# Revit family: Maxlogic détecteur en boîte arrière de montage en surface
name_source: partatom
category: Fire Alarm Devices
units: mm (PartAtom-declared; Revit-internal decimal feet)

## family parameters
Cut with Voids When Loaded = No
Host = Face
Maintain Annotation Orientation = Yes
OmniClass Number = 23.85.30.21
OmniClass Title = Environmental Detection/Registration
Part Type = Normal
Room Calculation Point = No
Round Connector Dimension = Use Diameter
Shared = No

## types (10) — shared parameters
Adresse ligne 1 = Şerifali Mahallesi Kutup Sokak No:27/1-2-4 Ümraniye TR-34775 İSTANBUL
Boîtier de montage en surface étanche = ML-0121
Couleur = Blanc
Deuxième Matèriel = Plastique
Durée de la garantie de pièces rechange = 2
Durée de la garantie travail = 2
Hauteur Nominal = 106 mm
Largeur Nominal = 51 mm
Longeur Nominal = 106 mm
Manuel d'Installation = https://mavilielektronik.com
Manufacturer = Mavili Elektronik Ticaret A.Ş.
Model = Maxlogic
Numéro de Fax = (+)90 216 466 45 10
Socle Compatible = ML-0140
Socle Compatible 2 = ML-0141
Socle Montage de Surlévé = ML-0150
Tempèrature de Fonctionnement = (-10°C) - (+50°C)
URL = https://www.mavili.com.tr
Voltage de fonctionnement (défaut) = 26 V/DC
zero-valued in all types: Cost, Default Elevation

## per-type parameters (varying)
| type | Cercle Chaleur | Cercle Multi Critère | Charger adresse d'appareil | Code de Performance | Code de Produit | Description | Détection de Radius | Matèriel Principe | Numéro de pose des travaux public | Poids | Sortie d'indicateur | Surface de Montage | Unité de durée de garantie | Voltage fonction d'opération |
| Maxlogic Conventionnelle Détecteur de fumée optique, en boîte arrière de montage en surface | No | No |  | EN 54-7 | ML-2110 | Conventionnelle Conventionnelle Détecteur de fumée optique, en boîte arrière de montage en surface | 6,2 m | Plastique Blanche PC/ABS | 832-106 | 140 gr | MG-4000 | Montage à Plafond | Ans | 10-30V/DC |
| Maxlogic Adressable Détecteur de fumée optique, en boîte arrière de montage en surface | No | No | Appareil d'adressage à Main | EN 54-7 | ML-1110 | Adressable Détecteur de fumée optique , en boîte arrière de montage en surface | 6,2 m | Plastique Blanche PC/ABS | 833-500 | 100 gr | MG-4000.A | Montage à Mur | Ans | 18-33V/DC |
| Maxlogic Adressable détecteur de fumée optique, en boîte arrière de montage en surface,Isolateur de Court-Circuit | No | No | Appareil d'adressage à Main | EN 54-7 / EN 54-17 | ML-1110.SCI | Adressable  Détecteur de fumée optique, en boîte arrière de montage en surface,Isolateur de Court-Circuit | 6,2 m | Plastique Blanche PC/ABS | 833-501 | 100 gr | MG-4000.A | Montage à Plafond | Ans | 18-33V/DC |
| Maxlogic Conventionnelle détecteur de chaleur fixe, en boîte arrière de montage en surface | Yes | No |  | EN 54-5 | ML-2120 | Conventionnelle  Détecteur de chaleur fixe, en boîte arrière de montage en surface | 4,5 m | Plastique Blanche PC/ABS | 832-102 | 135 gr | MG-4000 | Montage à Plafond | Ans | 10-30V/DC |
| Maxlogic Conventionnelle Détecteur de chaleur combiné , en boîte arrière de montage en surface | Yes | No |  | EN 54-5 | ML-2130 | Conventionnelle Détecteur de chaleur combiné , en boîte arrière de montage en surface | 4,5 m | Plastique Blanche PC/ABS | 832-103 | 135 gr | MG-4000 | Montage à Plafond | Year | 10-30V/DC |
| Maxlogic Adressable détecteur de chaleur combiné , en boîte arrière de montage en surface | Yes | No | Appareil d'adressage à Main | EN 54-5 | ML-1130 | Adressable détecteur de chaleur combiné , en boîte arrière de montage en surface | 4,5 m | Plastique Blanche PC/ABS | 833-520 | 95 gr | MG-4000.A | Montage à Plafond | Ans | 18-33V/DC |
| Maxlogic Adressable détecteur de chaleur combiné , en boîte arrière de montage en surface,Isolateur de Court-Circuit | Yes | No | Appareil d'adressage à Main | EN 54-5 / EN 54-17 | ML-1130.SCI | Adressable détecteur de chaleur combiné , en boîte arrière de montage en surface,Isolateur de Court-Circuit | 4,5 m | Plastique Blanche PC/ABS | 833-521 | 95 gr | MG-4000.A | Montage à Plafond | Ans | 18-33V/DC |
| Maxlogic Conventionnelle détecteur de multi-capteur ,en boîte arrière de montage en surface | Yes | Yes |  | EN 54-5 / EN 54-7 | ML-2140 | Conventionnelle détecteur de multi-capteur ,en boîte arrière de montage en surface | 4,5 m | Plastique Blanche PC/ABS | 832-109 | 141 gr | MG-4000 | Montage à Plafond | Ans | 10-30V/DC |
| Maxlogic Adressable Détecteur de multi-capteur, en boîte arrière de montage en surface | Yes | Yes | Appareil d'adressage à Main | EN 54-5 / EN 54-7 / EN 54-17 | ML-1140 | Maxlogic Adressable Détecteur de multi-capteur, en boîte arrière de montage en surface | 4,5 m | Plastique Blanche PC/ABS | 833-530 | 100 gr | MG-4000.A | Montage à Plafond | Ans | 18-33V/DC |
| Maxlogic Adressable Détecteur de multi-capteur, en boîte arrière de montage en surface,Isolateur de Court Circuit | Yes | Yes | Appareil d'adressage à Main | EN 54-5 / EN 54-7 / EN 54-17 | ML-1140.SCI | Adressable Détecteur de multi-capteur, en boîte arrière de montage en surface | 4,5 m | Plastique Blanche  PC/ABS | 833-531 | 100 gr | MG-4000.A | Montage à Plafond | Ans | 18-33V/DC |

## geometry (parser evidence)
native form markers: Sweep x1
no freeform markers — native parametric forms only
